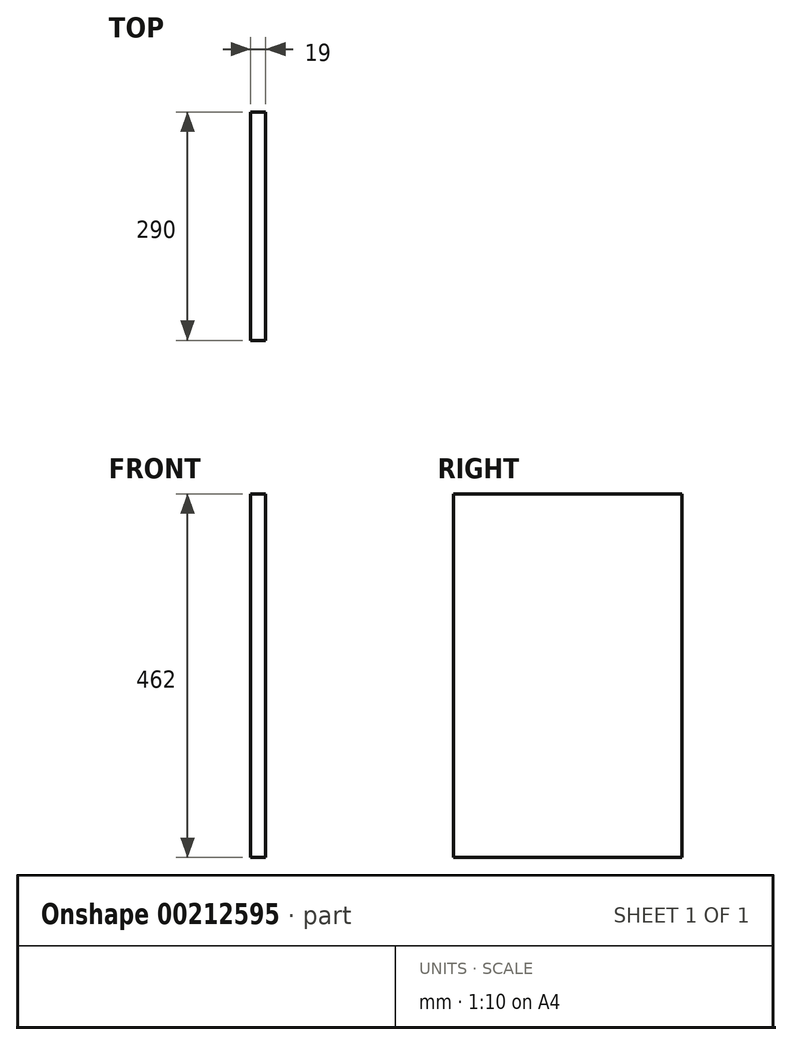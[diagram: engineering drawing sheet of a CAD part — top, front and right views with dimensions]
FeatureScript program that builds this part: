
annotation { "Feature Type Name" : "Feature", "Feature Type Description" : "" }
export const myFeature = defineFeature(function(context is Context, id is Id, definition is map)
    precondition{}
    {
        {
            var Q0;
            Q0=qCreatedBy(makeId("Right.planeOp"),FACE);
            var sketch = newSketch(context, id + "F0", { "sketchPlane" : qUnion([Q0])});
            skLineSegment(sketch, "E0.bottom", {"start": v(-145, 231) * mm, "end": v(145, 231) * mm});
            skLineSegment(sketch, "E0.top", {"start": v(-145, -231) * mm, "end": v(145, -231) * mm});
            skLineSegment(sketch, "E0.left", {"start": v(-145, 231) * mm, "end": v(-145, -231) * mm});
            skLineSegment(sketch, "E0.right", {"start": v(145, 231) * mm, "end": v(145, -231) * mm});
            skSolve(sketch);
        }
        {
            var Q0;
            Q0 = qSketchRegion(id + "F0", true);
            extrude(context, id + "F1", {"entities" : qUnion([Q0]), "depth" : 19 * mm});
        }
    });
